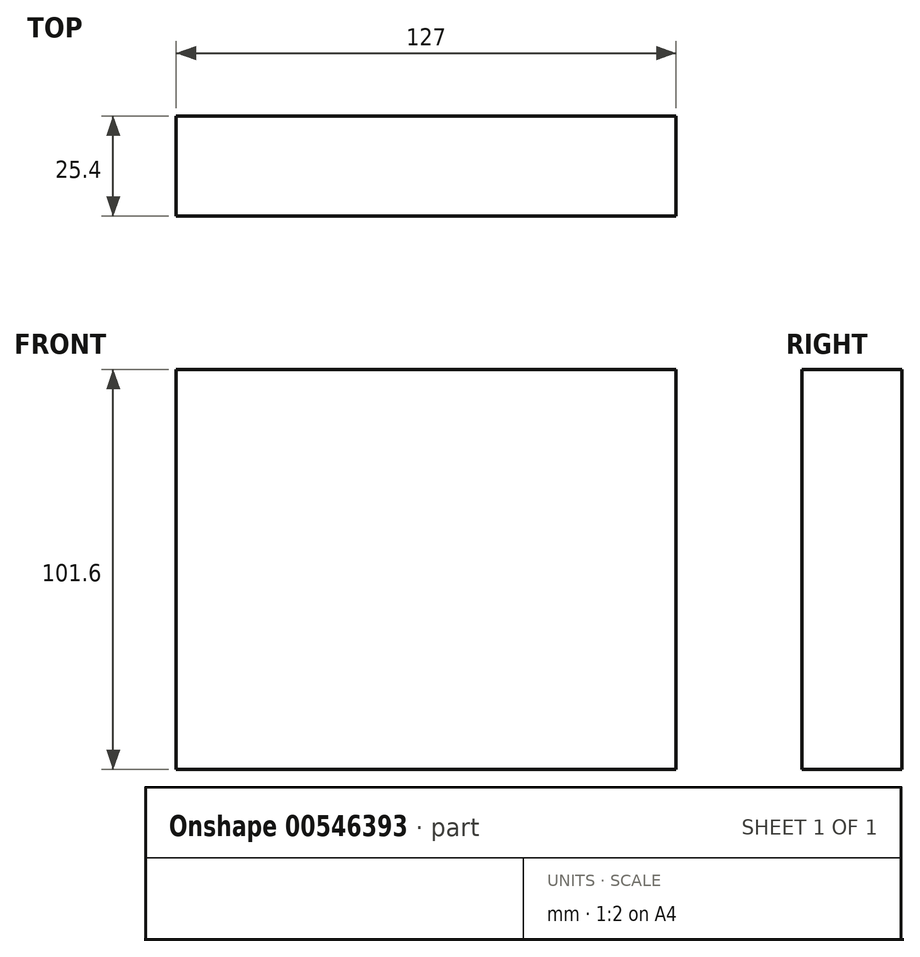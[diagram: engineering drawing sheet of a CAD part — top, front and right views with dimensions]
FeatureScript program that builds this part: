
annotation { "Feature Type Name" : "Feature", "Feature Type Description" : "" }
export const myFeature = defineFeature(function(context is Context, id is Id, definition is map)
    precondition{}
    {
        {
            var Q0;
            Q0=qCreatedBy(makeId("Front.planeOp"),FACE);
            var sketch = newSketch(context, id + "F0", { "sketchPlane" : qUnion([Q0])});
            skLineSegment(sketch, "E0.bottom", {"start": v(0, 0) * mm, "end": v(127, 0) * mm});
            skLineSegment(sketch, "E0.top", {"start": v(0, 101.6) * mm, "end": v(127, 101.6) * mm});
            skLineSegment(sketch, "E0.left", {"start": v(0, 0) * mm, "end": v(0, 101.6) * mm});
            skLineSegment(sketch, "E0.right", {"start": v(127, 0) * mm, "end": v(127, 101.6) * mm});
            skSolve(sketch);
        }
        {
            var Q0;
            Q0 = qSketchRegion(id + "F0", true);
            extrude(context, id + "F1", {"entities" : qUnion([Q0]), "depth" : 25.4 * mm, "offsetDistance" : 25.4 * mm});
        }
    });
